# Revit family: FU_Seat_LAPSE 0240TA
name_source: partatom
category: Furniture
units: mm (PartAtom-declared; Revit-internal decimal feet)

## family parameters
Always vertical = Yes
Cut with Voids When Loaded = No
OmniClass Number = 23.40.20.00
OmniClass Title = General Furniture and Specialties
Render Appearance Source = Family Geometry
Room Calculation Point = No
Shared = No
Work Plane-Based = No

## types (1)
- LAPSE 0240TA
    Default Elevation = 0 mm  [stored 0 ft]
    Depth = 760 mm  [stored 2.49344 ft]
    Description = Curved upholstered seat for the Lapse modular sofa system with a concave backrest at 45°.
    Height = 736 mm  [stored 2.4147 ft]
    Manufacturer = Sandler
    Model = LAPSE 0240TA
    URL = https://www.sandlerseating.com
    Width = 1080 mm  [stored 3.54331 ft]

note: [stored X ft] marks values corroborated as IEEE doubles in the binary element streams (Revit-internal decimal feet)

## geometry (parser evidence)
native form markers: Sweep x3
no freeform markers — native parametric forms only
